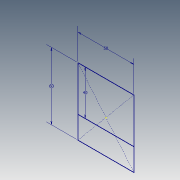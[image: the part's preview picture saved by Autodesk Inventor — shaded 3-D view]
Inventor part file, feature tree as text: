
AUTODESK INVENTOR PART (.ipt)
format: ipt  version: 2013 (Build 170138000, 138)  size: 62,464 bytes
history: native  units: mm
features: sketch x1
ambient origin geometry x8: Origin, YZ Plane, XZ Plane, XY Plane, X Axis, Y Axis, Z Axis, Center Point
feature tree (1):
  sketch  "Sketch1"  dims[d0=50.0mm d1=60.0mm d2=40.0mm]
